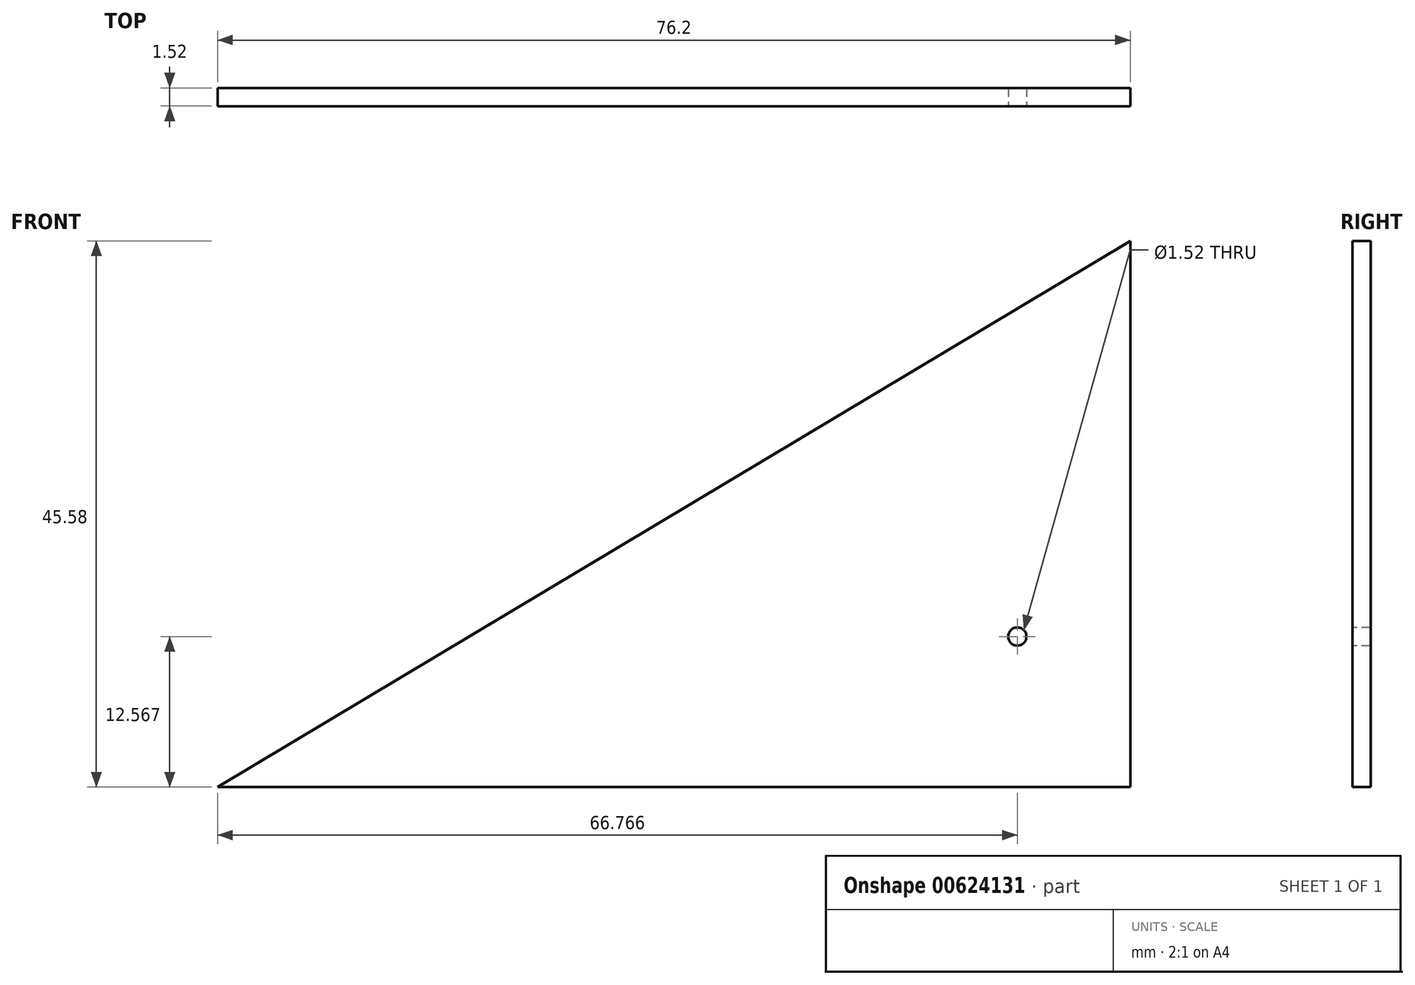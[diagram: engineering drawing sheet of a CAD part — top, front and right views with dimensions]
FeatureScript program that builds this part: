
annotation { "Feature Type Name" : "Feature", "Feature Type Description" : "" }
export const myFeature = defineFeature(function(context is Context, id is Id, definition is map)
    precondition{}
    {
        {
            var Q0;
            Q0=qCreatedBy(makeId("Front.planeOp"),FACE);
            var sketch = newSketch(context, id + "F0", { "sketchPlane" : qUnion([Q0])});
            skLineSegment(sketch, "E0.top", {"start": v(-0.45, -47.2) * mm, "end": v(75.75, -47.2) * mm});
            skLineSegment(sketch, "E0.right", {"start": v(75.75, -1.62) * mm, "end": v(75.75, -47.2) * mm});
            skLineSegment(sketch, "E1", {"start": v(75.75, -1.62) * mm, "end": v(-0.45, -47.2) * mm});
            skSolve(sketch);
        }
        {
            var Q0;
            Q0=makeQuery(id+"F0.imprint","IMPRINT",FACE,{"disambiguationData":[TD([[makeQuery(id+"F0.imprint","IMPRINT",EDGE,{"derivedFrom":sQuery(id+"F0.wireOp",EDGE,"E0.top")}),1.0]])]});
            extrude(context, id + "F1", {"entities" : qUnion([Q0]), "depth" : 1.52 * mm, "offsetDistance" : 25.4 * mm});
        }
        {
            var Q0;
            Q0=makeQuery(id+"F1.opExtrude","CAP_FACE",FACE,{"disambiguationData":[OSD([sQuery(id+"F0.wireOp",EDGE,"E0.top"),sQuery(id+"F0.wireOp",EDGE,"E0.right"),sQuery(id+"F0.wireOp",EDGE,"E1")])],"isStart":false});
            var sketch = newSketch(context, id + "F2", { "sketchPlane" : qUnion([Q0])});
            skCircle(sketch, "E2", {"center": v(66.32, -34.63) * mm, "radius": 0.76 * mm});
            skSolve(sketch);
        }
        {
            var Q0;
            Q0=makeQuery(id+"F2.imprint","IMPRINT",FACE,{"disambiguationData":[TD([[makeQuery(id+"F2.imprint","IMPRINT",EDGE,{"derivedFrom":sQuery(id+"F2.wireOp",EDGE,"E2")}),1.0]])]});
            extrude(context, id + "F3", {"entities" : qUnion([Q0]), "operationType" : NewBodyOperationType.REMOVE, "oppositeDirection" : true, "depth" : 83.49 * mm, "offsetDistance" : 25.4 * mm});
        }
    });
